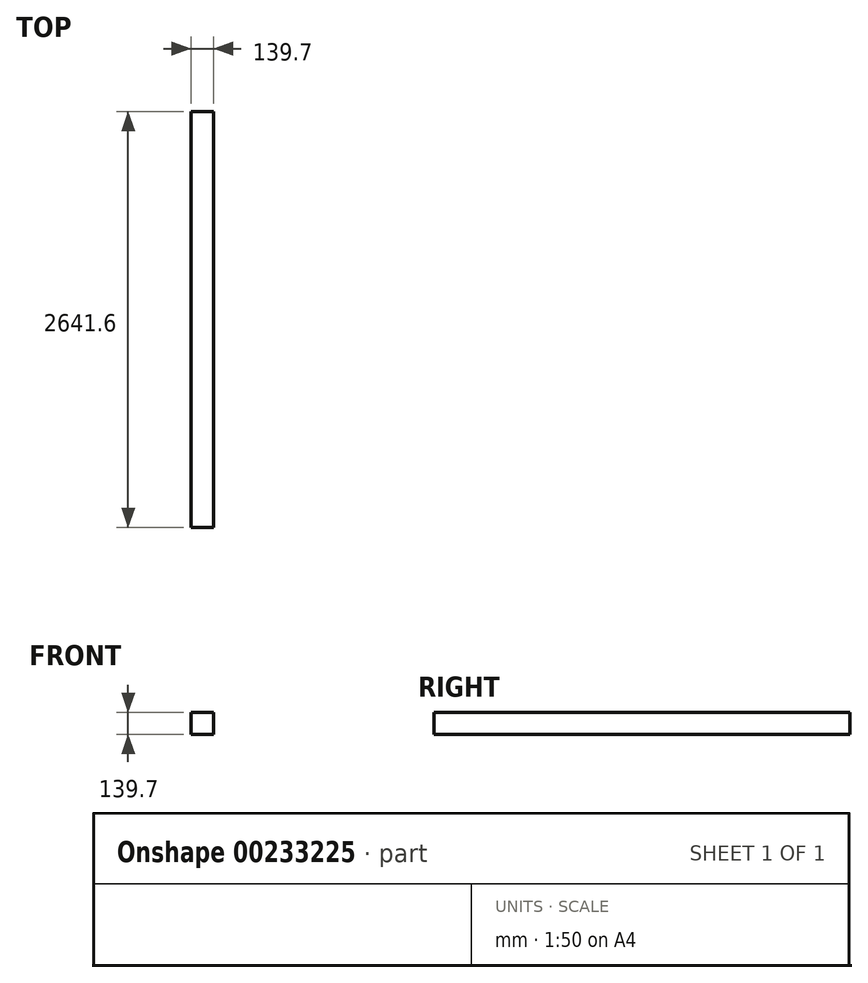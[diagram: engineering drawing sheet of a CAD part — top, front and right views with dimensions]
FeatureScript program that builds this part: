
annotation { "Feature Type Name" : "Feature", "Feature Type Description" : "" }
export const myFeature = defineFeature(function(context is Context, id is Id, definition is map)
    precondition{}
    {
        {
            var Q0;
            Q0=qCreatedBy(makeId("Front.planeOp"),FACE);
            var sketch = newSketch(context, id + "F0", { "sketchPlane" : qUnion([Q0])});
            skLineSegment(sketch, "E0.bottom", {"start": v(-62.89, 76.96) * mm, "end": v(76.81, 76.96) * mm});
            skLineSegment(sketch, "E0.top", {"start": v(-62.89, -62.74) * mm, "end": v(76.81, -62.74) * mm});
            skLineSegment(sketch, "E0.left", {"start": v(-62.89, 76.96) * mm, "end": v(-62.89, -62.74) * mm});
            skLineSegment(sketch, "E0.right", {"start": v(76.81, 76.96) * mm, "end": v(76.81, -62.74) * mm});
            skSolve(sketch);
        }
        {
            var Q0;
            Q0=qSketchRegion(id+"F0",true);
            extrude(context, id + "F1", {"entities" : qUnion([Q0]), "depth" : 2641.6 * mm});
        }
    });
